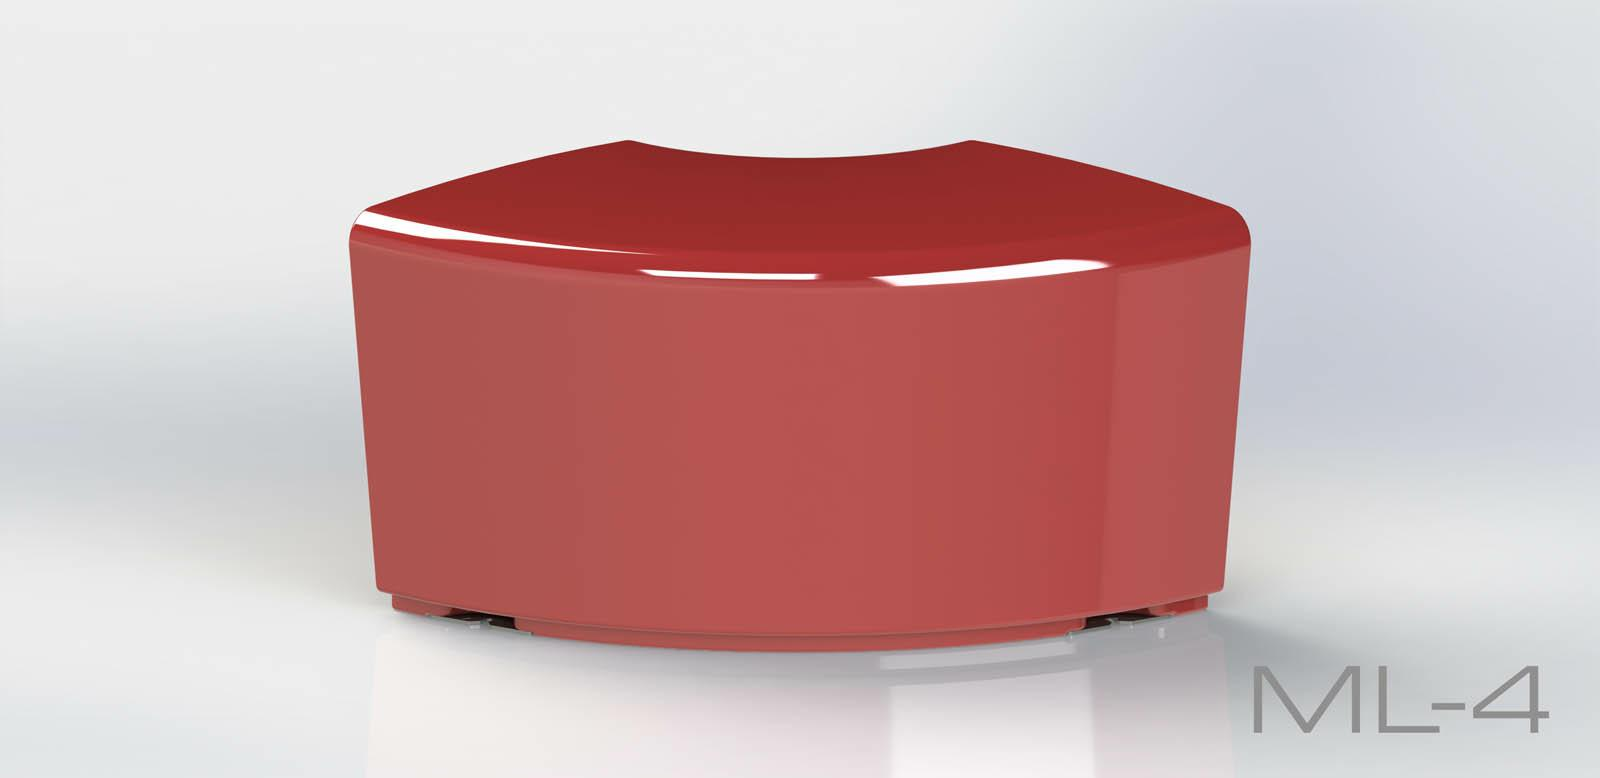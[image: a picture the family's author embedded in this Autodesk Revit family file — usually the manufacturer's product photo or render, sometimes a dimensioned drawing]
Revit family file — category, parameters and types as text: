
# Revit family: Modullaro ML 04
name_source: partatom
category: Meble
revit_build: Autodesk Revit 2018 (Build: 20190510_1515(x64)
units: mm (PartAtom-declared; Revit-internal decimal feet)

## family parameters
Numer OmniClass = 23.40.10.11.14
Obiekt nadrzędny = Powierzchnia
Punkt obliczania pomieszczeń = Nie
Tnij formami wycięć po wczytaniu = Nie
Tytuł OmniClass = Exterior Seating
Współdzielony = Nie

## types (1)
- Modullaro ML 04
    Domyślna rzędna = 1219 mm
    Długość = 747 mm  [stored 2.45079 ft]
    IfcExportAs = IfcFurnishingElement
    Komentarze do typu = Ławka
    Materiał - informacja = Szeroki wybór kolorów wg palety RAL. Istnieje również możliwość specjalnego wykonania kolorystycznego na indywidualne zapytanie klienta.
    Model = Modullaro ML 04
    Obraz typu = ML-4.jpg
    Producent = Astrini Design
    Szerokość = 494 mm
    Temepratura użytkowania = -40°C do 80°C, ( -40°F do 176°F )
    URL = http://astrini-design.pl
    Waga (szacunkowo) = 13.00 kg
    Wysokość = 500 mm  [stored 1.64042 ft]

note: [stored X ft] marks values corroborated as IEEE doubles in the binary element streams (Revit-internal decimal feet)
